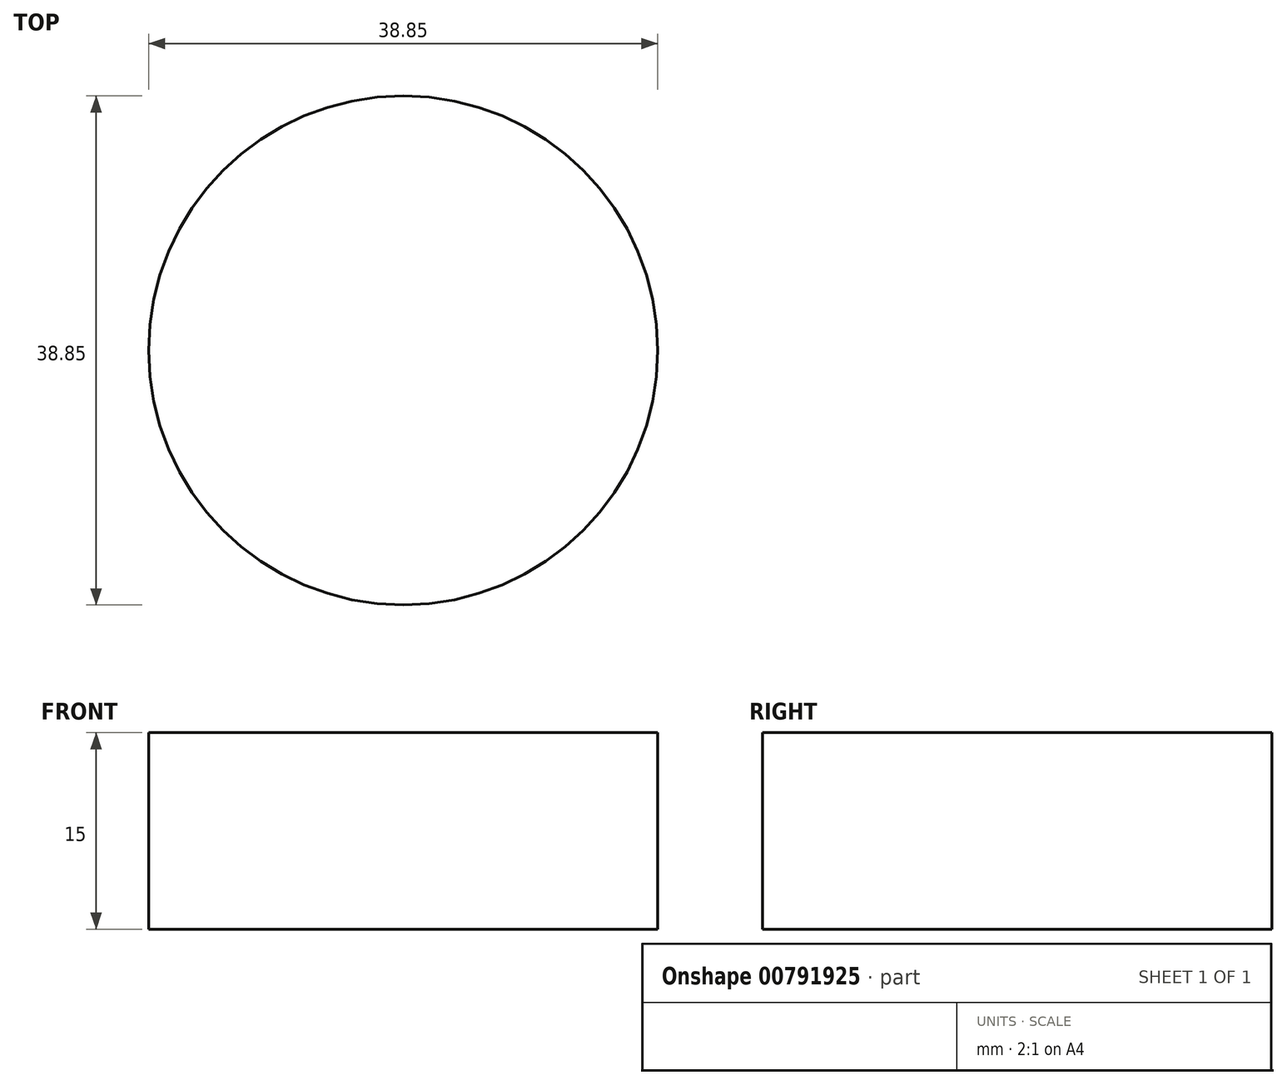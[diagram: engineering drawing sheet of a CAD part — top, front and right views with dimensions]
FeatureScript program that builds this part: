
annotation { "Feature Type Name" : "Feature", "Feature Type Description" : "" }
export const myFeature = defineFeature(function(context is Context, id is Id, definition is map)
    precondition{}
    {
        {
            var Q0;
            Q0=qCreatedBy(makeId("Top.planeOp"),FACE);
            var sketch = newSketch(context, id + "F0", { "sketchPlane" : qUnion([Q0])});
            skCircle(sketch, "E0", {"center": v(0.12, 0.12) * mm, "radius": 19.42 * mm});
            skLineSegment(sketch, "E1", {"start": v(-41.51, 0.56) * mm, "end": v(-25.98, 0.64) * mm});
            skLineSegment(sketch, "E2", {"start": v(-34.56, 9.29) * mm, "end": v(-33.2, -9.32) * mm});
            skSolve(sketch);
        }
        {
            var Q0;
            Q0 = qSketchRegion(id + "F0", true);
            extrude(context, id + "F1", {"entities" : qUnion([Q0]), "depth" : 15 * mm, "offsetDistance" : 25.4 * mm});
        }
    });
